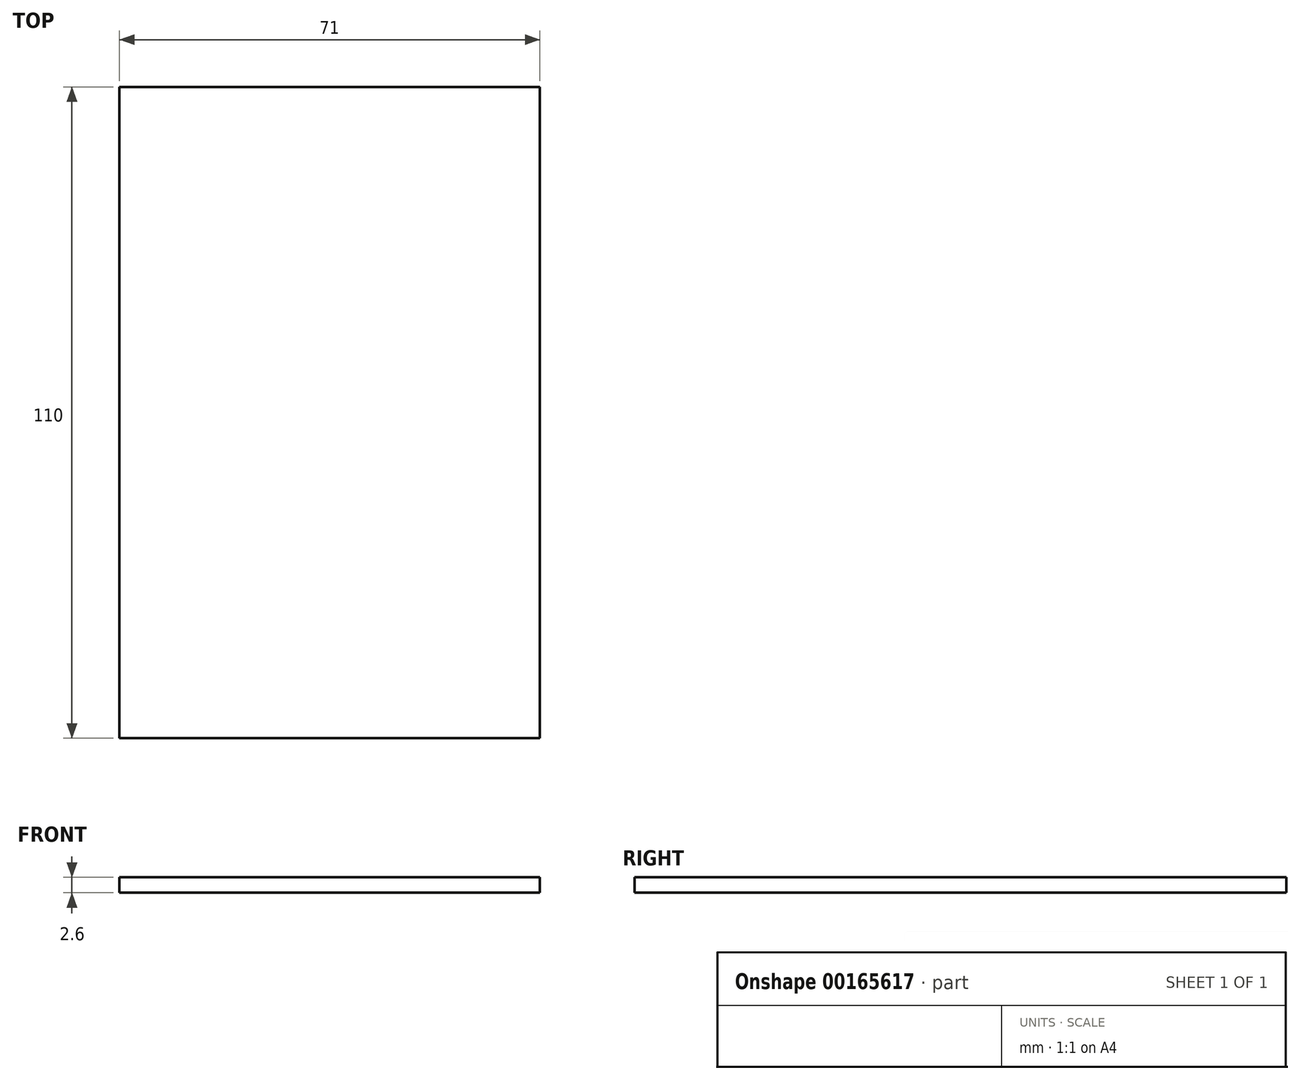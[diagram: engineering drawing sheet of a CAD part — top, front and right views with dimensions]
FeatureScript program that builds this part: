
annotation { "Feature Type Name" : "Feature", "Feature Type Description" : "" }
export const myFeature = defineFeature(function(context is Context, id is Id, definition is map)
    precondition{}
    {
        {
            var Q0;
            Q0=qCreatedBy(makeId("Top.planeOp"),FACE);
            var sketch = newSketch(context, id + "F0", { "sketchPlane" : qUnion([Q0])});
            skLineSegment(sketch, "E0.bottom", {"start": v(-35.5, 55) * mm, "end": v(35.5, 55) * mm});
            skLineSegment(sketch, "E0.top", {"start": v(-35.5, -55) * mm, "end": v(35.5, -55) * mm});
            skLineSegment(sketch, "E0.left", {"start": v(-35.5, 55) * mm, "end": v(-35.5, -55) * mm});
            skLineSegment(sketch, "E0.right", {"start": v(35.5, 55) * mm, "end": v(35.5, -55) * mm});
            skPoint(sketch, "E0.middle", {"position": v(0, 0) * mm});
            skSolve(sketch);
        }
        {
            var Q0;
            Q0=makeQuery(id+"F0.imprint","IMPRINT",FACE,{"disambiguationData":[TD([[makeQuery(id+"F0.imprint","IMPRINT",EDGE,{"derivedFrom":sQuery(id+"F0.wireOp",EDGE,"E0.bottom")}),-1.0]])]});
            extrude(context, id + "F1", {"entities" : qUnion([Q0]), "depth" : 2.6 * mm});
        }
    });
